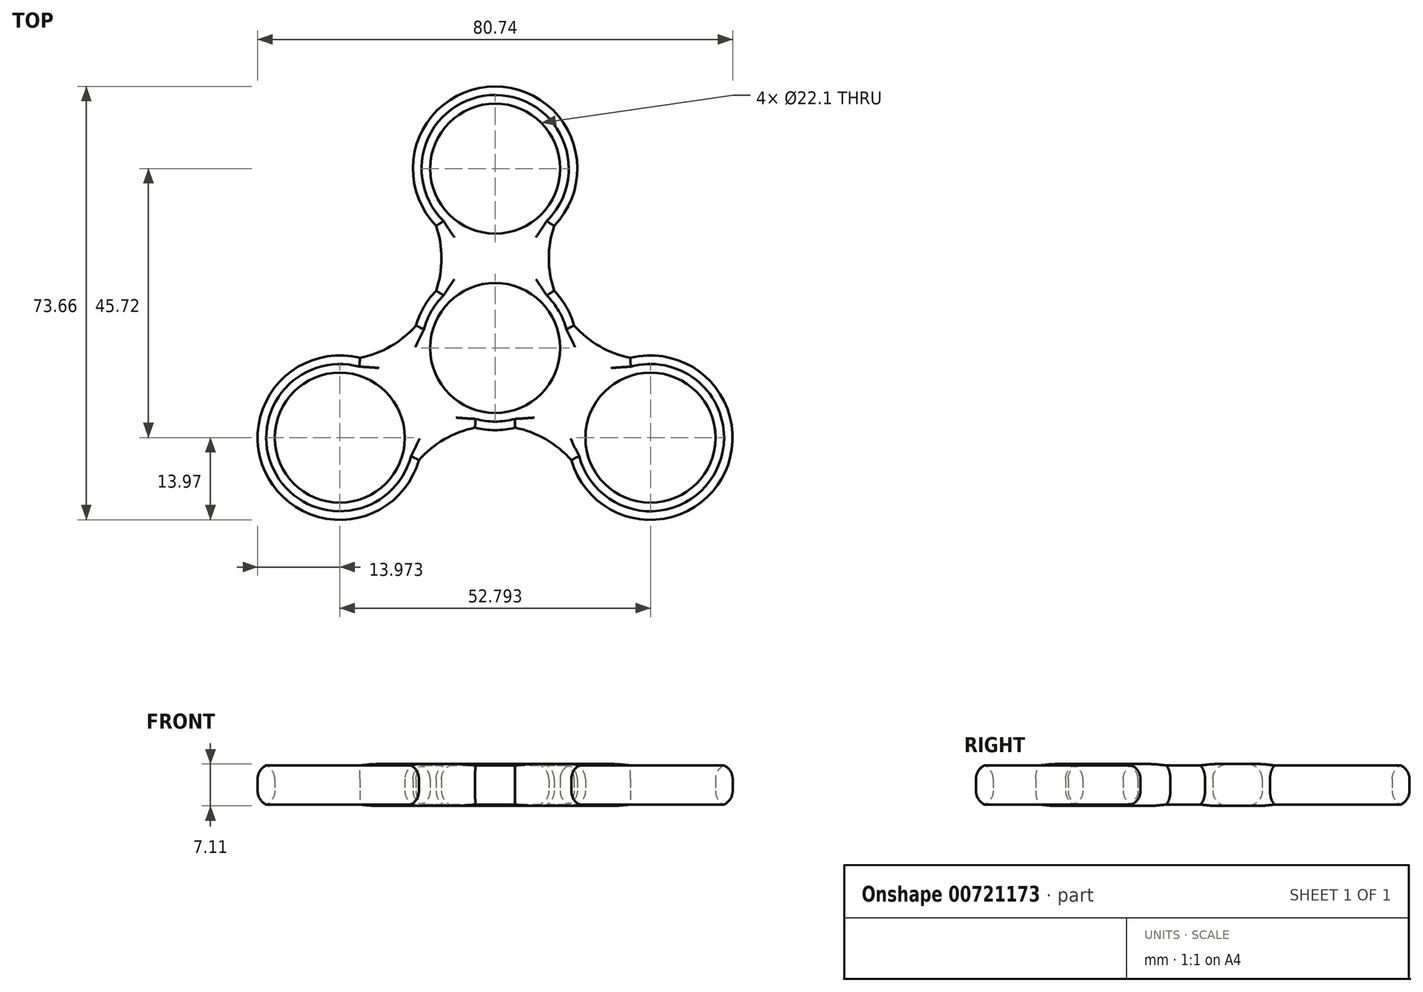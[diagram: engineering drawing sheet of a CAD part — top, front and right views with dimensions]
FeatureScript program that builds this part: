
annotation { "Feature Type Name" : "Feature", "Feature Type Description" : "" }
export const myFeature = defineFeature(function(context is Context, id is Id, definition is map)
    precondition{}
    {
        {
            var Q0;
            Q0=qCreatedBy(makeId("Top.planeOp"),FACE);
            var sketch = newSketch(context, id + "F0", { "sketchPlane" : qUnion([Q0])});
            skCircle(sketch, "E0", {"center": v(0, 0) * mm, "radius": 11.05 * mm});
            skCircle(sketch, "E1", {"center": v(0, 0) * mm, "radius": 13.97 * mm});
            skLineSegment(sketch, "E2", {"start": v(0, 0) * mm, "end": v(0, 30.48) * mm});
            skCircle(sketch, "E3", {"center": v(0, 30.48) * mm, "radius": 11.05 * mm});
            skCircle(sketch, "E4.1.0", {"center": v(-26.4, -15.24) * mm, "radius": 11.05 * mm});
            skCircle(sketch, "E4.2.0", {"center": v(26.4, -15.24) * mm, "radius": 11.05 * mm});
            skCircle(sketch, "E5", {"center": v(0, 30.48) * mm, "radius": 13.97 * mm});
            skCircle(sketch, "E6.1.0", {"center": v(-26.4, -15.24) * mm, "radius": 13.97 * mm});
            skCircle(sketch, "E6.2.0", {"center": v(26.4, -15.24) * mm, "radius": 13.97 * mm});
            skLineSegment(sketch, "E7", {"start": v(0, 0) * mm, "end": v(-26.4, 15.24) * mm});
            skArc(sketch, "E8", {"start": v(-29.8, -1.7) * mm, "mid": v(-11.44, 6.6) * mm, "end": v(-13.43, 26.65) * mm});
            skArc(sketch, "E9.1.0", {"start": v(16.36, -24.96) * mm, "mid": v(0, -13.21) * mm, "end": v(-16.36, -24.96) * mm});
            skArc(sketch, "E9.2.0", {"start": v(13.43, 26.65) * mm, "mid": v(11.44, 6.6) * mm, "end": v(29.8, -1.7) * mm});
            skSolve(sketch);
        }
        {
            var Q0;
            Q0 = qSketchRegion(id + "F0", true);
            extrude(context, id + "F1", {"entities" : qUnion([Q0]), "depth" : 7.11 * mm, "offsetDistance" : 25.4 * mm});
        }
        {
            var Q0;
            Q0=makeQuery(id+"F1.opExtrude","CAP_FACE",FACE,{"disambiguationData":[OSD([sQuery(id+"F0.wireOp",EDGE,"E0"),sQuery(id+"F0.wireOp",EDGE,"E1"),sQuery(id+"F0.wireOp",EDGE,"E3"),sQuery(id+"F0.wireOp",EDGE,"E4.1.0"),sQuery(id+"F0.wireOp",EDGE,"E4.2.0"),sQuery(id+"F0.wireOp",EDGE,"E5"),sQuery(id+"F0.wireOp",EDGE,"E6.1.0"),sQuery(id+"F0.wireOp",EDGE,"E6.2.0"),sQuery(id+"F0.wireOp",EDGE,"E8"),sQuery(id+"F0.wireOp",EDGE,"E9.1.0"),sQuery(id+"F0.wireOp",EDGE,"E9.2.0")])],"isStart":false});
            var Q1;
            Q1=makeQuery(id+"F1.opExtrude","CAP_FACE",FACE,{"disambiguationData":[OSD([sQuery(id+"F0.wireOp",EDGE,"E0"),sQuery(id+"F0.wireOp",EDGE,"E1"),sQuery(id+"F0.wireOp",EDGE,"E3"),sQuery(id+"F0.wireOp",EDGE,"E4.1.0"),sQuery(id+"F0.wireOp",EDGE,"E4.2.0"),sQuery(id+"F0.wireOp",EDGE,"E5"),sQuery(id+"F0.wireOp",EDGE,"E6.1.0"),sQuery(id+"F0.wireOp",EDGE,"E6.2.0"),sQuery(id+"F0.wireOp",EDGE,"E8"),sQuery(id+"F0.wireOp",EDGE,"E9.1.0"),sQuery(id+"F0.wireOp",EDGE,"E9.2.0")])],"isStart":true});
            fillet(context, id + "F2", {"entities" : qUnion([Q0, Q1]), "radius" : 2.54 * mm, "tangentPropagation" : true, "allowEdgeOverflow" : false});
        }
    });
